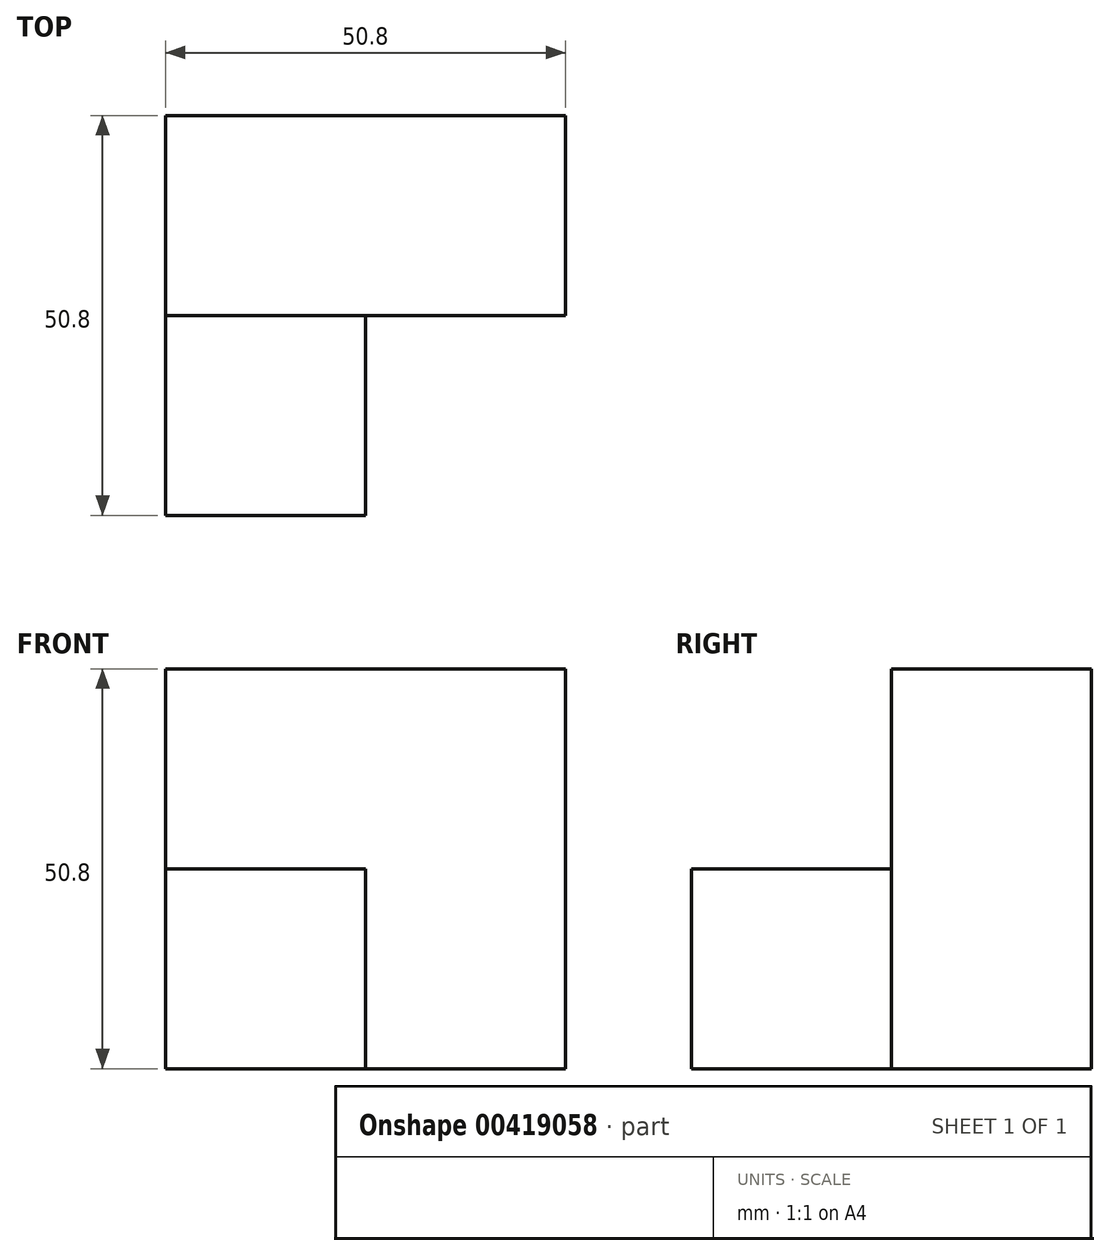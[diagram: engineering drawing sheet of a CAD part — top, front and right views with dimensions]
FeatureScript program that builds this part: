
annotation { "Feature Type Name" : "Feature", "Feature Type Description" : "" }
export const myFeature = defineFeature(function(context is Context, id is Id, definition is map)
    precondition{}
    {
        {
            var Q0;
            Q0=qCreatedBy(makeId("Front.planeOp"),FACE);
            var sketch = newSketch(context, id + "F0", { "sketchPlane" : qUnion([Q0])});
            skLineSegment(sketch, "E0", {"start": v(0, 0) * mm, "end": v(0, 50.8) * mm});
            skLineSegment(sketch, "E1", {"start": v(0, 0) * mm, "end": v(-50.8, 0) * mm});
            skLineSegment(sketch, "E2", {"start": v(-50.8, 0) * mm, "end": v(-50.8, 50.8) * mm});
            skLineSegment(sketch, "E3", {"start": v(0, 50.8) * mm, "end": v(-50.8, 50.8) * mm});
            skSolve(sketch);
        }
        {
            var Q0;
            Q0 = qSketchRegion(id + "F0", true);
            extrude(context, id + "F1", {"entities" : qUnion([Q0]), "depth" : 25.4 * mm});
        }
        {
            var Q0;
            Q0=makeQuery(id+"F1.opExtrude","CAP_FACE",FACE,{"disambiguationData":[OSD([sQuery(id+"F0.wireOp",EDGE,"E0"),sQuery(id+"F0.wireOp",EDGE,"E1"),sQuery(id+"F0.wireOp",EDGE,"E2"),sQuery(id+"F0.wireOp",EDGE,"E3")])],"isStart":false});
            var sketch = newSketch(context, id + "F2", { "sketchPlane" : qUnion([Q0])});
            skLineSegment(sketch, "E4", {"start": v(-50.8, 0) * mm, "end": v(-25.4, 0) * mm});
            skLineSegment(sketch, "E5", {"start": v(-25.4, 0) * mm, "end": v(-25.4, 25.4) * mm});
            skLineSegment(sketch, "E6", {"start": v(-25.4, 25.4) * mm, "end": v(-50.8, 25.4) * mm});
            skLineSegment(sketch, "E7", {"start": v(-50.8, 25.4) * mm, "end": v(-50.8, 0) * mm});
            skSolve(sketch);
        }
        {
            var Q0;
            Q0 = qSketchRegion(id + "F2", true);
            extrude(context, id + "F3", {"entities" : qUnion([Q0]), "operationType" : NewBodyOperationType.ADD, "depth" : 25.4 * mm});
        }
    });
